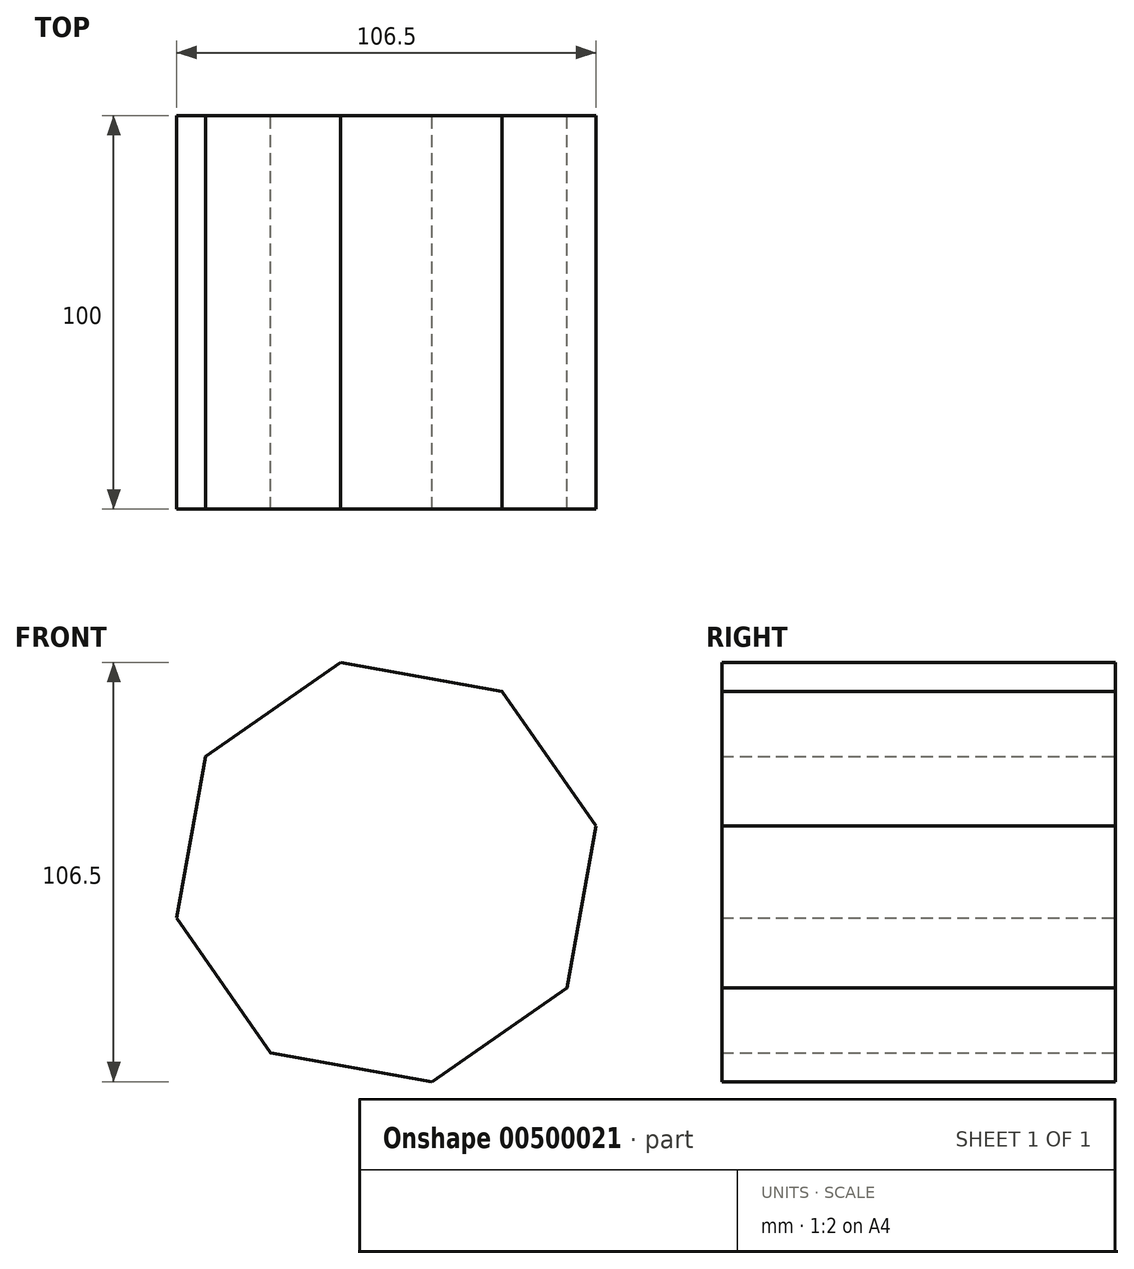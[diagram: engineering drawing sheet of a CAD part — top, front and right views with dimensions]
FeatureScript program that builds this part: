
annotation { "Feature Type Name" : "Feature", "Feature Type Description" : "" }
export const myFeature = defineFeature(function(context is Context, id is Id, definition is map)
    precondition{}
    {
        {
            var Q0;
            Q0=qCreatedBy(makeId("Front.planeOp"),FACE);
            var sketch = newSketch(context, id + "F0", { "sketchPlane" : qUnion([Q0])});
            skCircle(sketch, "E0.cCircle", {"center": v(0, 0) * mm, "radius": 54.51 * mm, "construction": true});
            skLineSegment(sketch, "E0.0", {"start": v(-45.9, 29.4) * mm, "end": v(-11.66, 53.25) * mm});
            skLineSegment(sketch, "E0.1", {"start": v(-11.66, 53.25) * mm, "end": v(29.4, 45.9) * mm});
            skLineSegment(sketch, "E0.2", {"start": v(29.4, 45.9) * mm, "end": v(53.25, 11.66) * mm});
            skLineSegment(sketch, "E0.3", {"start": v(53.25, 11.66) * mm, "end": v(45.9, -29.4) * mm});
            skLineSegment(sketch, "E0.4", {"start": v(45.9, -29.4) * mm, "end": v(11.66, -53.25) * mm});
            skLineSegment(sketch, "E0.5", {"start": v(11.66, -53.25) * mm, "end": v(-29.4, -45.9) * mm});
            skLineSegment(sketch, "E0.6", {"start": v(-29.4, -45.9) * mm, "end": v(-53.25, -11.66) * mm});
            skLineSegment(sketch, "E0.7", {"start": v(-53.25, -11.66) * mm, "end": v(-45.9, 29.4) * mm});
            skSolve(sketch);
        }
        {
            var Q0;
            Q0=makeQuery(id+"F0.imprint","IMPRINT",FACE,{"disambiguationData":[TD([[makeQuery(id+"F0.imprint","IMPRINT",EDGE,{"derivedFrom":sQuery(id+"F0.wireOp",EDGE,"E0.0")}),-1.0]])]});
            extrude(context, id + "F1", {"entities" : qUnion([Q0]), "endBound" : BoundingType.SYMMETRIC, "depth" : 100 * mm});
        }
    });
